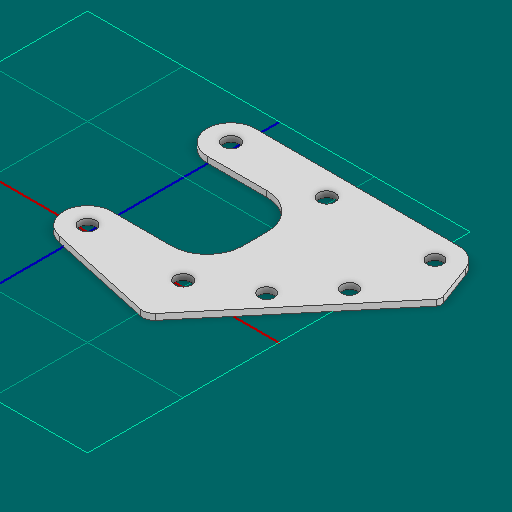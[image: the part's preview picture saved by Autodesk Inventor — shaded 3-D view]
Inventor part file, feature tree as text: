
AUTODESK INVENTOR PART (.ipt)
format: ipt  version: 2025 (Build 290162000, 162)  size: 152,064 bytes
history: native  units: in
note: dims shown in document units (in); Inventor stores cm internally (conversion verified against a paired STEP export)
features: other x6, sketch x1
ambient origin geometry x8: Origin, YZ Plane, XZ Plane, XY Plane, X Axis, Y Axis, Z Axis, Center Point
bodies: Solid1 (feature_tree)
feature tree (7):
  other  "funel_gusset_mirrored.ipt"
  other  "Blocks"
  other  "main"
  other  "Solid1::funel_gusset_mirrored.ipt"
  other  "TaggingFeature1"
  sketch  "Sketch1"  dims[d0=0.3937in d1=0.5in d6=0.375in d8=0.164in d9=0.0625in d14=0.164in d15=0.615in d17=0.125in]
  other  "main:1"
